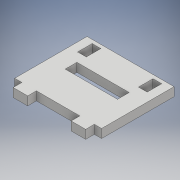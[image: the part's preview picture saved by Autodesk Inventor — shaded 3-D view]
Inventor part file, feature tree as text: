
AUTODESK INVENTOR PART (.ipt)
format: ipt  version: 2017 (Build 210142000, 142)  size: 122,368 bytes
history: native  units: mm
features: extrude x1, sketch x1
ambient origin geometry x8: Origin, YZ Plane, XZ Plane, XY Plane, X Axis, Y Axis, Z Axis, Center Point
bodies: Solide1 (feature_tree)
feature tree (2):
  extrude  "Extrusion1"  Depth=50.0mm
  sketch  "Esquisse1"
